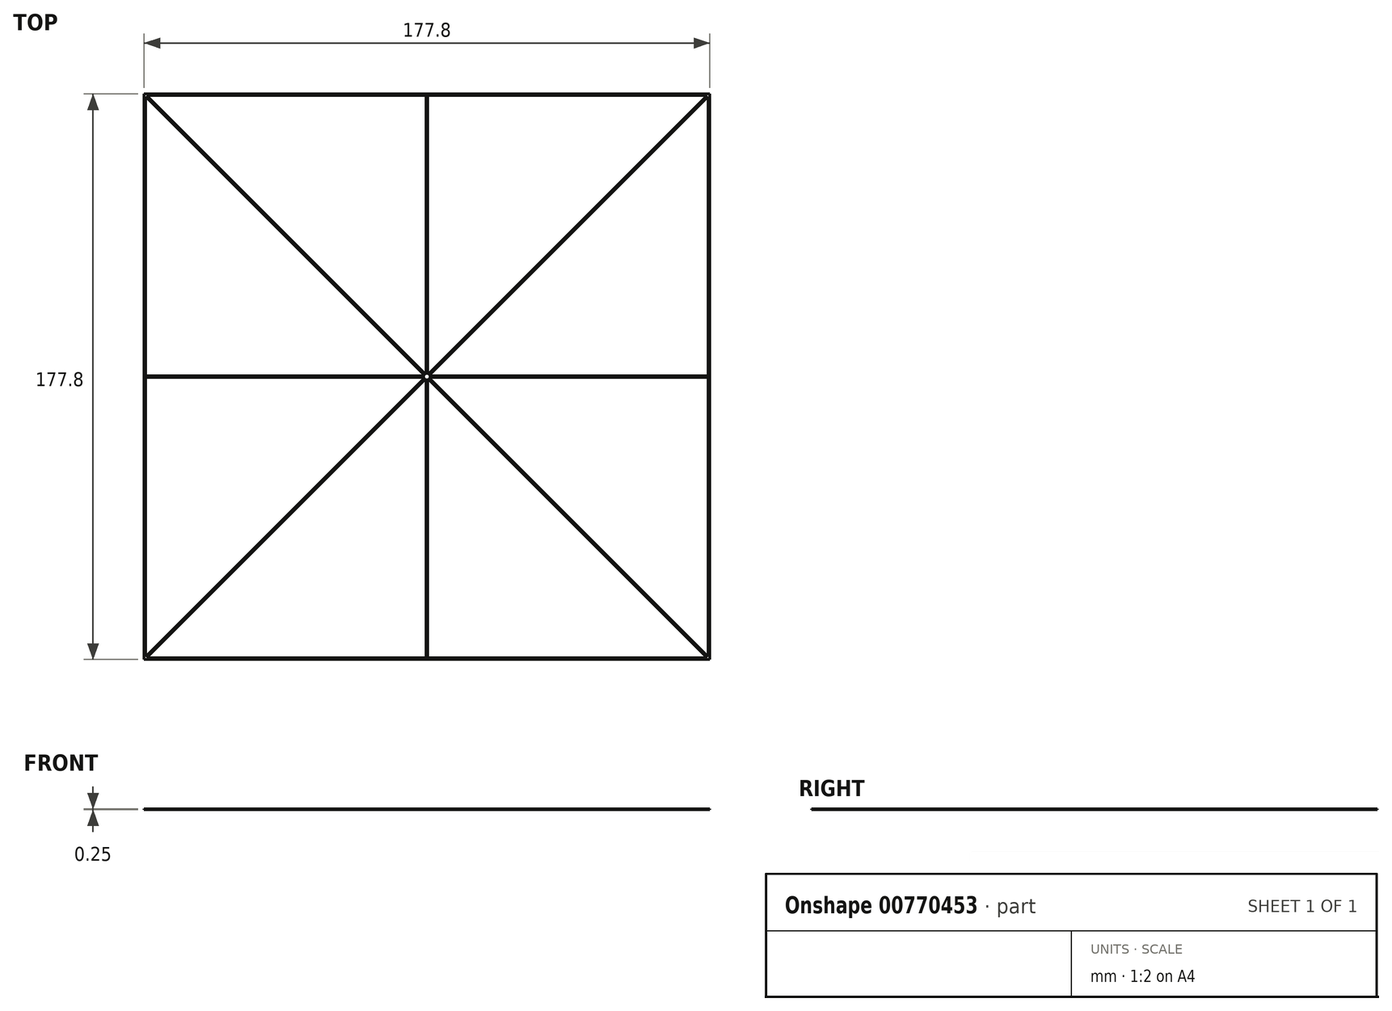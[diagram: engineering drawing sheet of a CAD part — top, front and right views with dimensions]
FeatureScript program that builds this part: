
annotation { "Feature Type Name" : "Feature", "Feature Type Description" : "" }
export const myFeature = defineFeature(function(context is Context, id is Id, definition is map)
    precondition{}
    {
        {
            var Q0;
            Q0=qCreatedBy(makeId("Top.planeOp"),FACE);
            var sketch = newSketch(context, id + "F0", { "sketchPlane" : qUnion([Q0])});
            skLineSegment(sketch, "E0.bottom", {"start": v(-88.9, -88.9) * mm, "end": v(88.9, -88.9) * mm, "construction": true});
            skLineSegment(sketch, "E0.top", {"start": v(-88.9, 88.9) * mm, "end": v(88.9, 88.9) * mm, "construction": true});
            skLineSegment(sketch, "E0.left", {"start": v(-88.9, -88.9) * mm, "end": v(-88.9, 88.9) * mm, "construction": true});
            skLineSegment(sketch, "E0.right", {"start": v(88.9, -88.9) * mm, "end": v(88.9, 88.9) * mm, "construction": true});
            skPoint(sketch, "E0.middle", {"position": v(0, 0) * mm});
            skLineSegment(sketch, "E1.bottom", {"start": v(-88.4, -88.4) * mm, "end": v(88.4, -88.4) * mm, "construction": true});
            skLineSegment(sketch, "E1.top", {"start": v(-88.4, 88.4) * mm, "end": v(88.4, 88.4) * mm, "construction": true});
            skLineSegment(sketch, "E1.left", {"start": v(-88.4, -88.4) * mm, "end": v(-88.4, 88.4) * mm, "construction": true});
            skLineSegment(sketch, "E1.right", {"start": v(88.4, -88.4) * mm, "end": v(88.4, 88.4) * mm, "construction": true});
            skLineSegment(sketch, "E2", {"start": v(0, 0) * mm, "end": v(0, 88.4) * mm, "construction": true});
            skLineSegment(sketch, "E3", {"start": v(-88.4, 88.4) * mm, "end": v(88.4, -88.4) * mm, "construction": true});
            skLineSegment(sketch, "E4", {"start": v(-88.4, -88.4) * mm, "end": v(88.4, 88.4) * mm, "construction": true});
            skLineSegment(sketch, "E5", {"start": v(0, 0) * mm, "end": v(-88.4, 0) * mm, "construction": true});
            skLineSegment(sketch, "E6", {"start": v(-0.25, 88.4) * mm, "end": v(-0.25, -88.4) * mm, "construction": true});
            skLineSegment(sketch, "E7", {"start": v(0.25, 88.4) * mm, "end": v(0.25, -88.4) * mm, "construction": true});
            skLineSegment(sketch, "E8", {"start": v(88.03, 88.4) * mm, "end": v(-88.4, -88.03) * mm, "construction": true});
            skLineSegment(sketch, "E9.0", {"start": v(88.4, 88.03) * mm, "end": v(-88.03, -88.4) * mm, "construction": true});
            skLineSegment(sketch, "E10.0", {"start": v(-88.4, 88.03) * mm, "end": v(88.03, -88.4) * mm, "construction": true});
            skLineSegment(sketch, "E11.0", {"start": v(-88.03, 88.4) * mm, "end": v(88.4, -88.03) * mm, "construction": true});
            skLineSegment(sketch, "E12.0", {"start": v(88.4, 0.25) * mm, "end": v(-88.4, 0.25) * mm, "construction": true});
            skLineSegment(sketch, "E13.0", {"start": v(88.4, -0.25) * mm, "end": v(-88.4, -0.25) * mm, "construction": true});
            skSolve(sketch);
        }
        {
            var Q0;
            Q0=qCreatedBy(makeId("Top.planeOp"),FACE);
            var sketch = newSketch(context, id + "F1", { "sketchPlane" : qUnion([Q0])});
            skPoint(sketch, "E14.middle", {"position": v(0, 0) * mm});
            skLineSegment(sketch, "E15.0", {"start": v(-88.9, 88.9) * mm, "end": v(88.9, 88.9) * mm});
            skLineSegment(sketch, "E16.1", {"start": v(88.9, -88.9) * mm, "end": v(88.9, 88.9) * mm});
            skLineSegment(sketch, "E17.1", {"start": v(-88.9, -88.9) * mm, "end": v(88.9, -88.9) * mm});
            skLineSegment(sketch, "E18.0", {"start": v(-88.9, -88.9) * mm, "end": v(-88.9, 88.9) * mm});
            skLineSegment(sketch, "E19.0", {"start": v(-88.03, 88.4) * mm, "end": v(-0.25, 88.4) * mm});
            skLineSegment(sketch, "E20.0", {"start": v(-0.25, 88.4) * mm, "end": v(-0.25, 0.61) * mm});
            skLineSegment(sketch, "E21.0", {"start": v(0.25, 88.4) * mm, "end": v(0.25, 0.61) * mm});
            skLineSegment(sketch, "E22.0", {"start": v(-88.4, -88.03) * mm, "end": v(-88.4, -0.25) * mm});
            skLineSegment(sketch, "E23.0", {"start": v(-88.03, 88.4) * mm, "end": v(-0.25, 0.61) * mm});
            skLineSegment(sketch, "E24.0", {"start": v(-88.4, 88.03) * mm, "end": v(-0.61, 0.25) * mm});
            skLineSegment(sketch, "E25.0", {"start": v(88.4, -88.03) * mm, "end": v(88.4, -0.25) * mm});
            skLineSegment(sketch, "E26.0", {"start": v(-88.03, -88.4) * mm, "end": v(-0.25, -88.4) * mm});
            skLineSegment(sketch, "E27.0", {"start": v(88.4, 88.03) * mm, "end": v(0.61, 0.25) * mm});
            skLineSegment(sketch, "E28.0", {"start": v(88.03, 88.4) * mm, "end": v(0.25, 0.61) * mm});
            skLineSegment(sketch, "E29.0", {"start": v(88.4, 0.25) * mm, "end": v(0.61, 0.25) * mm});
            skLineSegment(sketch, "E30.0", {"start": v(88.4, -0.25) * mm, "end": v(0.61, -0.25) * mm});
            skLineSegment(sketch, "E31.trimOffspring", {"start": v(0.25, 88.4) * mm, "end": v(88.03, 88.4) * mm});
            skLineSegment(sketch, "E32.trimOffspring", {"start": v(0.25, -88.4) * mm, "end": v(88.03, -88.4) * mm});
            skLineSegment(sketch, "E33.trimOffspring", {"start": v(88.4, 0.25) * mm, "end": v(88.4, 88.03) * mm});
            skLineSegment(sketch, "E34.trimOffspring", {"start": v(-88.4, 0.25) * mm, "end": v(-88.4, 88.03) * mm});
            skLineSegment(sketch, "E35.trimOffspring", {"start": v(-0.61, 0.25) * mm, "end": v(-88.4, 0.25) * mm});
            skLineSegment(sketch, "E36.trimOffspring", {"start": v(0.61, -0.25) * mm, "end": v(88.4, -88.03) * mm});
            skLineSegment(sketch, "E37.trimOffspring", {"start": v(0.25, -0.61) * mm, "end": v(0.25, -88.4) * mm});
            skLineSegment(sketch, "E38.trimOffspring", {"start": v(0.25, -0.61) * mm, "end": v(88.03, -88.4) * mm});
            skLineSegment(sketch, "E39.trimOffspring", {"start": v(-0.25, -0.61) * mm, "end": v(-88.03, -88.4) * mm});
            skLineSegment(sketch, "E40.trimOffspring", {"start": v(-0.61, -0.25) * mm, "end": v(-88.4, -88.03) * mm});
            skLineSegment(sketch, "E41.trimOffspring", {"start": v(-0.61, -0.25) * mm, "end": v(-88.4, -0.25) * mm});
            skLineSegment(sketch, "E42.trimOffspring", {"start": v(-0.25, -0.61) * mm, "end": v(-0.25, -88.4) * mm});
            skPoint(sketch, "E43.orphan", {"position": v(-88.4, 88.4) * mm});
            skPoint(sketch, "E44.orphan", {"position": v(88.4, 88.4) * mm});
            skPoint(sketch, "E45.orphan", {"position": v(88.4, -88.4) * mm});
            skPoint(sketch, "E46.orphan", {"position": v(-88.4, -88.4) * mm});
            skSolve(sketch);
        }
        {
            var Q0;
            Q0=qSketchRegion(id+"F1",true);
            extrude(context, id + "F2", {"entities" : qUnion([Q0]), "depth" : 0.25 * mm, "offsetDistance" : 25.4 * mm});
        }
    });
